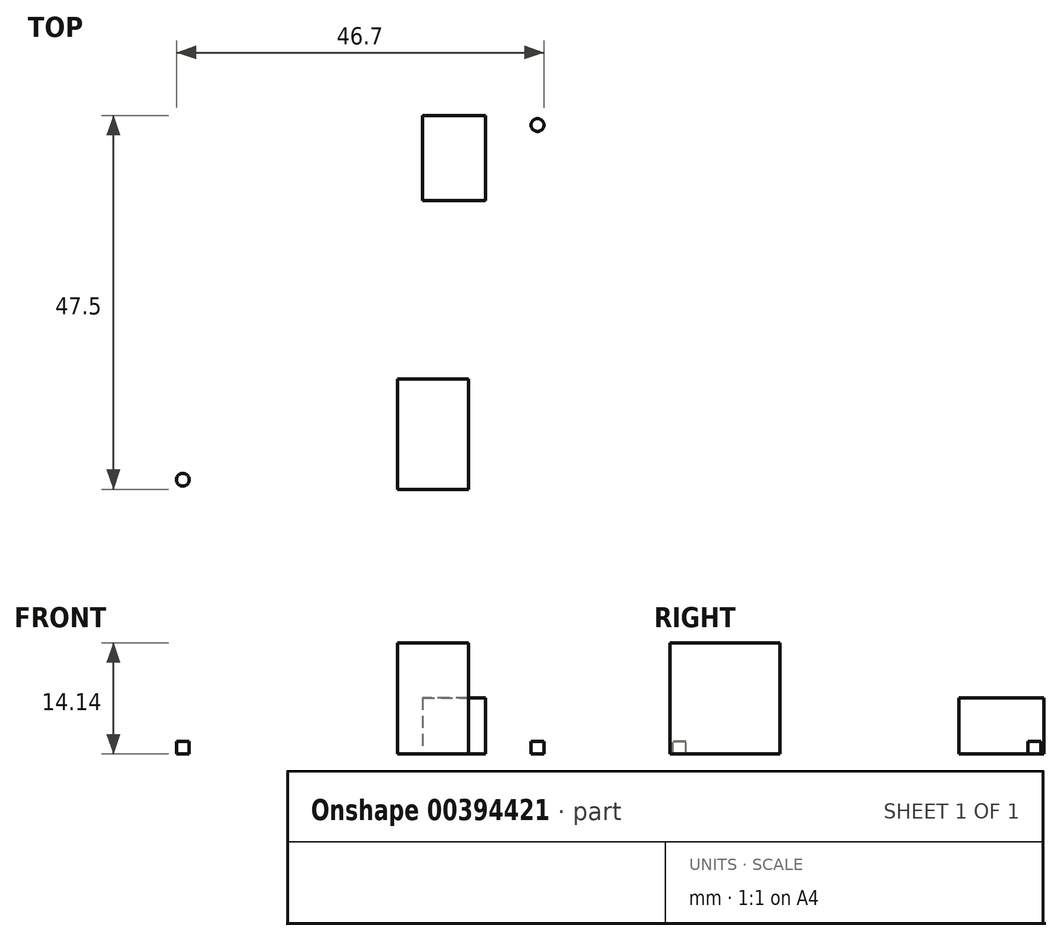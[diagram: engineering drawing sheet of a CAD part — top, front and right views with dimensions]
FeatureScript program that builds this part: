
annotation { "Feature Type Name" : "Feature", "Feature Type Description" : "" }
export const myFeature = defineFeature(function(context is Context, id is Id, definition is map)
    precondition{}
    {
        {
            var Q0;
            Q0=qCreatedBy(makeId("Top.planeOp"),FACE);
            var sketch = newSketch(context, id + "F0", { "sketchPlane" : qUnion([Q0])});
            skLineSegment(sketch, "E0.bottom", {"start": v(23.75, -23.75) * mm, "end": v(-23.75, -23.75) * mm});
            skLineSegment(sketch, "E0.top", {"start": v(23.75, 23.75) * mm, "end": v(-23.75, 23.75) * mm});
            skLineSegment(sketch, "E0.left", {"start": v(23.75, -23.75) * mm, "end": v(23.75, 23.75) * mm});
            skLineSegment(sketch, "E0.right", {"start": v(-23.75, -23.75) * mm, "end": v(-23.75, 23.75) * mm});
            skPoint(sketch, "E0.middle", {"position": v(0, 0) * mm});
            skSolve(sketch);
        }
        {
            var Q0;
            Q0 = qSketchRegion(id + "F0", true);
            extrude(context, id + "F1", {"entities" : qUnion([Q0]), "depth" : 1.6 * mm});
        }
        {
            var Q0;
            Q0=makeQuery(id+"F1.opExtrude","CAP_FACE",FACE,{"disambiguationData":[OSD([sQuery(id+"F0.wireOp",EDGE,"E0.bottom"),sQuery(id+"F0.wireOp",EDGE,"E0.top"),sQuery(id+"F0.wireOp",EDGE,"E0.left"),sQuery(id+"F0.wireOp",EDGE,"E0.right")])],"isStart":false});
            var sketch = newSketch(context, id + "F2", { "sketchPlane" : qUnion([Q0])});
            skLineSegment(sketch, "E1", {"start": v(23.75, -23.75) * mm, "end": v(13.75, -23.75) * mm});
            skLineSegment(sketch, "E2", {"start": v(13.75, -23.75) * mm, "end": v(13.75, -9.75) * mm});
            skLineSegment(sketch, "E3", {"start": v(13.75, -9.75) * mm, "end": v(4.75, -9.75) * mm});
            skLineSegment(sketch, "E4", {"start": v(4.75, -9.75) * mm, "end": v(4.75, -23.75) * mm});
            skLineSegment(sketch, "E5", {"start": v(4.75, -23.75) * mm, "end": v(13.75, -23.75) * mm});
            skLineSegment(sketch, "E6", {"start": v(23.75, 23.75) * mm, "end": v(7.95, 23.75) * mm});
            skLineSegment(sketch, "E7", {"start": v(7.95, 23.75) * mm, "end": v(7.95, 12.94) * mm});
            skLineSegment(sketch, "E8", {"start": v(7.95, 12.94) * mm, "end": v(15.95, 12.94) * mm});
            skLineSegment(sketch, "E9", {"start": v(15.95, 12.94) * mm, "end": v(15.95, 23.75) * mm});
            skLineSegment(sketch, "E10", {"start": v(15.95, 23.75) * mm, "end": v(7.95, 23.75) * mm});
            skLineSegment(sketch, "E11", {"start": v(-23.75, 23.1) * mm, "end": v(-22.53, 23.1) * mm});
            skLineSegment(sketch, "E12", {"start": v(-22.53, 22.53) * mm, "end": v(-22.53, 23.1) * mm});
            skLineSegment(sketch, "E13", {"start": v(-22.56, 22.53) * mm, "end": v(-22.53, 22.53) * mm});
            skCircle(sketch, "E14", {"center": v(-22.53, 22.53) * mm, "radius": 0.81 * mm});
            skCircle(sketch, "E15.MirrorC", {"center": v(22.53, 22.53) * mm, "radius": 0.81 * mm});
            skCircle(sketch, "E16.MirrorC", {"center": v(-22.53, -22.53) * mm, "radius": 0.81 * mm});
            skCircle(sketch, "E17.MirrorC", {"center": v(22.53, -22.53) * mm, "radius": 0.81 * mm});
            skSolve(sketch);
        }
        {
            var Q0;
            Q0=makeQuery(id+"F2.imprint","IMPRINT",FACE,{"disambiguationData":[TD([[makeQuery(id+"F2.imprint","IMPRINT",EDGE,{"derivedFrom":sQuery(id+"F2.wireOp",EDGE,"E2")}),1.0]])]});
            extrude(context, id + "F3", {"entities" : qUnion([Q0]), "operationType" : NewBodyOperationType.ADD, "depth" : 12.54 * mm});
        }
        {
            var Q0;
            Q0=makeQuery(id+"F2.imprint","IMPRINT",FACE,{"disambiguationData":[TD([[makeQuery(id+"F2.imprint","IMPRINT",EDGE,{"derivedFrom":sQuery(id+"F2.wireOp",EDGE,"E7")}),1.0]])]});
            extrude(context, id + "F4", {"entities" : qUnion([Q0]), "operationType" : NewBodyOperationType.ADD, "depth" : 5.54 * mm});
        }
        {
            var Q0;
            Q0=makeQuery(id+"F2.imprint","IMPRINT",FACE,{"disambiguationData":[TD([[makeQuery(id+"F2.imprint","IMPRINT",EDGE,{"derivedFrom":sQuery(id+"F2.wireOp",EDGE,"E16.MirrorC")}),-1.0]])]});
            var Q1;
            Q1=makeQuery(id+"F2.imprint","IMPRINT",FACE,{"disambiguationData":[TD([[makeQuery(id+"F2.imprint","IMPRINT",EDGE,{"derivedFrom":sQuery(id+"F2.wireOp",EDGE,"E17.MirrorC")}),1.0]])]});
            var Q2;
            Q2=makeQuery(id+"F2.imprint","IMPRINT",FACE,{"disambiguationData":[TD([[makeQuery(id+"F2.imprint","IMPRINT",EDGE,{"derivedFrom":sQuery(id+"F2.wireOp",EDGE,"E15.MirrorC")}),-1.0]])]});
            var Q3;
            Q3=makeQuery(id+"F2.imprint","IMPRINT",FACE,{"disambiguationData":[TD([[makeQuery(id+"F2.imprint","IMPRINT",EDGE,{"derivedFrom":sQuery(id+"F2.wireOp",EDGE,"E14")}),1.0]])]});
            extrude(context, id + "F5", {"entities" : qUnion([Q0, Q1, Q2, Q3]), "operationType" : NewBodyOperationType.REMOVE, "oppositeDirection" : true, "depth" : 1.6 * mm});
        }
    });
